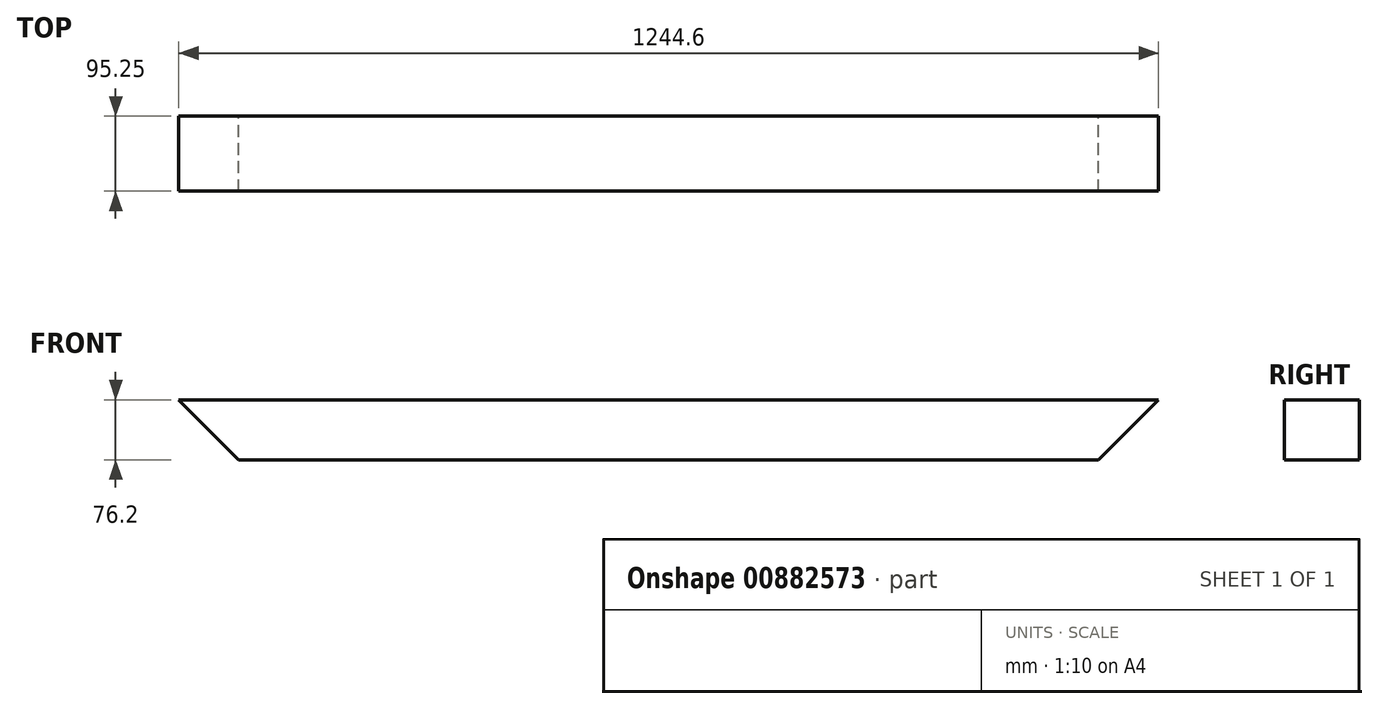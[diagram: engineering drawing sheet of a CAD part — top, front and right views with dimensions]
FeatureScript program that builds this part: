
annotation { "Feature Type Name" : "Feature", "Feature Type Description" : "" }
export const myFeature = defineFeature(function(context is Context, id is Id, definition is map)
    precondition{}
    {
        {
            var Q0;
            Q0=qCreatedBy(makeId("Right.planeOp"),FACE);
            var sketch = newSketch(context, id + "F0", { "sketchPlane" : qUnion([Q0])});
            skLineSegment(sketch, "E0.bottom", {"start": v(0, 0) * mm, "end": v(-95.25, 0) * mm});
            skLineSegment(sketch, "E0.top", {"start": v(0, -76.2) * mm, "end": v(-95.25, -76.2) * mm});
            skLineSegment(sketch, "E0.left", {"start": v(0, 0) * mm, "end": v(0, -76.2) * mm});
            skLineSegment(sketch, "E0.right", {"start": v(-95.25, 0) * mm, "end": v(-95.25, -76.2) * mm});
            skSolve(sketch);
        }
        {
            var Q0;
            Q0=makeQuery(id+"F0.imprint","IMPRINT",FACE,{"disambiguationData":[TD([[makeQuery(id+"F0.imprint","IMPRINT",EDGE,{"derivedFrom":sQuery(id+"F0.wireOp",EDGE,"E0.bottom")}),1.0]])]});
            extrude(context, id + "F1", {"entities" : qUnion([Q0]), "depth" : 1244.6 * mm, "offsetDistance" : 25.4 * mm});
        }
        {
            var Q0;
            Q0=makeQuery(id+"F1.opExtrude","SWEPT_FACE",FACE,{"disambiguationData":[OSD([sQuery(id+"F0.wireOp",EDGE,"E0.left")])]});
            var sketch = newSketch(context, id + "F2", { "sketchPlane" : qUnion([Q0])});
            skLineSegment(sketch, "E1", {"start": v(-1244.6, 0) * mm, "end": v(-1244.6, -76.2) * mm});
            skLineSegment(sketch, "E2", {"start": v(-1244.6, -76.2) * mm, "end": v(-1168.4, -76.2) * mm});
            skLineSegment(sketch, "E3", {"start": v(-1168.4, -76.2) * mm, "end": v(-1244.6, 0) * mm});
            skLineSegment(sketch, "E4", {"start": v(0, 0) * mm, "end": v(0, -76.2) * mm});
            skLineSegment(sketch, "E5", {"start": v(0, -76.2) * mm, "end": v(-76.2, -76.2) * mm});
            skLineSegment(sketch, "E6", {"start": v(-76.2, -76.2) * mm, "end": v(0, 0) * mm});
            skSolve(sketch);
        }
        {
            var Q0;
            Q0 = qSketchRegion(id + "F2", true);
            extrude(context, id + "F3", {"entities" : qUnion([Q0]), "operationType" : NewBodyOperationType.REMOVE, "endBound" : BoundingType.THROUGH_ALL, "oppositeDirection" : true, "depth" : 25.4 * mm, "offsetDistance" : 25.4 * mm});
        }
    });
